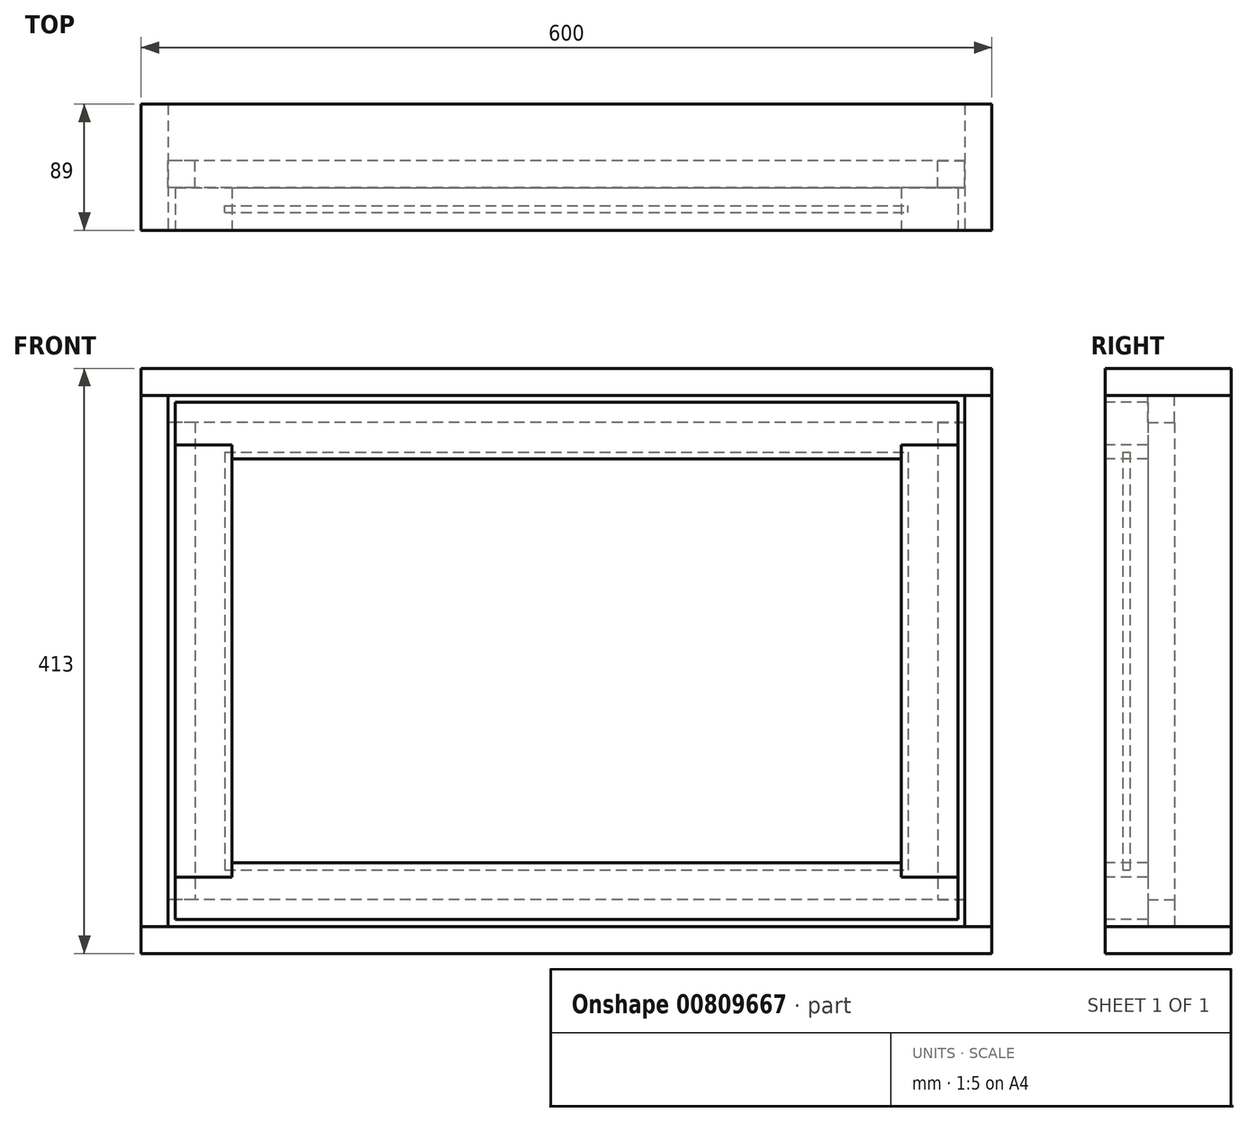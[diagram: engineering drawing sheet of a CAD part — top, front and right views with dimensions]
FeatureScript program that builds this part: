
annotation { "Feature Type Name" : "Feature", "Feature Type Description" : "" }
export const myFeature = defineFeature(function(context is Context, id is Id, definition is map)
    precondition{}
    {
        {
            assignVariable(context, id + "F0", {"name" : "D", "anyValue" : 89});
        }
        {
            var Q0;
            Q0=qCreatedBy(makeId("Front.planeOp"),FACE);
            var sketch = newSketch(context, id + "F1", { "sketchPlane" : qUnion([Q0])});
            skLineSegment(sketch, "E0.bottom", {"start": v(300, 206.5) * mm, "end": v(-300, 206.5) * mm});
            skLineSegment(sketch, "E0.top", {"start": v(300, -206.5) * mm, "end": v(-300, -206.5) * mm});
            skLineSegment(sketch, "E0.left", {"start": v(300, 206.5) * mm, "end": v(300, -206.5) * mm});
            skLineSegment(sketch, "E0.right", {"start": v(-300, 206.5) * mm, "end": v(-300, -206.5) * mm});
            skPoint(sketch, "E0.middle", {"position": v(0, 0) * mm});
            skSolve(sketch);
        }
        {
            var Q0;
            Q0=makeQuery(id+"F1.imprint","IMPRINT",FACE,{"disambiguationData":[TD([[makeQuery(id+"F1.imprint","IMPRINT",EDGE,{"derivedFrom":sQuery(id+"F1.wireOp",EDGE,"E0.bottom")}),1.0]])]});
            extrude(context, id + "F2", {"entities" : qUnion([Q0]), "oppositeDirection" : true, "depth" : (getVariable(context, 'D')) * mm, "offsetDistance" : 25 * mm});
        }
        {
            var Q0;
            Q0=makeQuery(id+"F2.opExtrude","CAP_FACE",FACE,{"disambiguationData":[OSD([sQuery(id+"F1.wireOp",EDGE,"E0.bottom"),sQuery(id+"F1.wireOp",EDGE,"E0.top"),sQuery(id+"F1.wireOp",EDGE,"E0.left"),sQuery(id+"F1.wireOp",EDGE,"E0.right")])],"isStart":true});
            var sketch = newSketch(context, id + "F3", { "sketchPlane" : qUnion([Q0])});
            skLineSegment(sketch, "E1.bottom", {"start": v(-300, -206.5) * mm, "end": v(300, -206.5) * mm});
            skLineSegment(sketch, "E1.top", {"start": v(-300, -187.5) * mm, "end": v(300, -187.5) * mm});
            skLineSegment(sketch, "E1.left", {"start": v(-300, -206.5) * mm, "end": v(-300, -187.5) * mm});
            skLineSegment(sketch, "E1.right", {"start": v(300, -206.5) * mm, "end": v(300, -187.5) * mm});
            skLineSegment(sketch, "E2.bottom", {"start": v(-300, 206.5) * mm, "end": v(300, 206.5) * mm});
            skLineSegment(sketch, "E2.top", {"start": v(-300, 187.5) * mm, "end": v(300, 187.5) * mm});
            skLineSegment(sketch, "E2.left", {"start": v(-300, 206.5) * mm, "end": v(-300, 187.5) * mm});
            skLineSegment(sketch, "E2.right", {"start": v(300, 206.5) * mm, "end": v(300, 187.5) * mm});
            skLineSegment(sketch, "E3.bottom", {"start": v(-300, 187.5) * mm, "end": v(-281, 187.5) * mm});
            skLineSegment(sketch, "E3.top", {"start": v(-300, -187.5) * mm, "end": v(-281, -187.5) * mm});
            skLineSegment(sketch, "E3.left", {"start": v(-300, 187.5) * mm, "end": v(-300, -187.5) * mm});
            skLineSegment(sketch, "E3.right", {"start": v(-281, 187.5) * mm, "end": v(-281, -187.5) * mm});
            skLineSegment(sketch, "E4.bottom", {"start": v(300, 187.5) * mm, "end": v(281, 187.5) * mm});
            skLineSegment(sketch, "E4.top", {"start": v(300, -187.5) * mm, "end": v(281, -187.5) * mm});
            skLineSegment(sketch, "E4.left", {"start": v(300, 187.5) * mm, "end": v(300, -187.5) * mm});
            skLineSegment(sketch, "E4.right", {"start": v(281, 187.5) * mm, "end": v(281, -187.5) * mm});
            skSolve(sketch);
        }
        {
            var Q0;
            Q0=makeQuery(id+"F3.imprint","IMPRINT",FACE,{"disambiguationData":[TD([[makeQuery(id+"F3.imprint","IMPRINT",EDGE,{"derivedFrom":sQuery(id+"F3.wireOp",EDGE,"E1.bottom")}),-1.0]])]});
            var Q1;
            Q1=makeQuery(id+"F2.opExtrude","CAP_FACE",FACE,{"disambiguationData":[OSD([sQuery(id+"F1.wireOp",EDGE,"E0.bottom"),sQuery(id+"F1.wireOp",EDGE,"E0.top"),sQuery(id+"F1.wireOp",EDGE,"E0.left"),sQuery(id+"F1.wireOp",EDGE,"E0.right")])],"isStart":false});
            extrude(context, id + "F4", {"entities" : qUnion([Q0]), "endBound" : BoundingType.UP_TO_SURFACE, "oppositeDirection" : true, "depth" : 25 * mm, "endBoundEntityFace" : qUnion([Q1]), "offsetDistance" : 25 * mm});
        }
        {
            var Q0;
            Q0=makeQuery(id+"F3.imprint","IMPRINT",FACE,{"disambiguationData":[TD([[makeQuery(id+"F3.imprint","IMPRINT",EDGE,{"derivedFrom":sQuery(id+"F3.wireOp",EDGE,"E2.bottom")}),1.0]])]});
            var Q1;
            Q1=makeQuery(id+"F2.opExtrude","CAP_FACE",FACE,{"disambiguationData":[OSD([sQuery(id+"F1.wireOp",EDGE,"E0.bottom"),sQuery(id+"F1.wireOp",EDGE,"E0.top"),sQuery(id+"F1.wireOp",EDGE,"E0.left"),sQuery(id+"F1.wireOp",EDGE,"E0.right")])],"isStart":false});
            extrude(context, id + "F5", {"entities" : qUnion([Q0]), "endBound" : BoundingType.UP_TO_SURFACE, "oppositeDirection" : true, "depth" : 25 * mm, "endBoundEntityFace" : qUnion([Q1]), "offsetDistance" : 25 * mm});
        }
        {
            var Q0;
            {var subQ2=sQuery(id+"F3.wireOp",EDGE,"E3.left");Q0=makeQuery(id+"F3.imprint","IMPRINT",FACE,{"disambiguationData":[TD([[makeQuery(id+"F3.imprint","IMPRINT",EDGE,{"derivedFrom":subQ2}),1.0]])]});}
            var Q1;
            Q1=makeQuery(id+"F2.opExtrude","CAP_FACE",FACE,{"disambiguationData":[OSD([sQuery(id+"F1.wireOp",EDGE,"E0.bottom"),sQuery(id+"F1.wireOp",EDGE,"E0.top"),sQuery(id+"F1.wireOp",EDGE,"E0.left"),sQuery(id+"F1.wireOp",EDGE,"E0.right")])],"isStart":false});
            extrude(context, id + "F6", {"entities" : qUnion([Q0]), "endBound" : BoundingType.UP_TO_SURFACE, "oppositeDirection" : true, "depth" : 25 * mm, "endBoundEntityFace" : qUnion([Q1]), "offsetDistance" : 25 * mm});
        }
        {
            var Q0;
            {var subQ0=sQuery(id+"F3.wireOp",EDGE,"E4.left");Q0=makeQuery(id+"F3.imprint","IMPRINT",FACE,{"disambiguationData":[TD([[makeQuery(id+"F3.imprint","IMPRINT",EDGE,{"derivedFrom":subQ0}),-1.0]])]});}
            var Q1;
            Q1=makeQuery(id+"F2.opExtrude","CAP_FACE",FACE,{"disambiguationData":[OSD([sQuery(id+"F1.wireOp",EDGE,"E0.bottom"),sQuery(id+"F1.wireOp",EDGE,"E0.top"),sQuery(id+"F1.wireOp",EDGE,"E0.left"),sQuery(id+"F1.wireOp",EDGE,"E0.right")])],"isStart":false});
            extrude(context, id + "F7", {"entities" : qUnion([Q0]), "endBound" : BoundingType.UP_TO_SURFACE, "oppositeDirection" : true, "depth" : 25 * mm, "endBoundEntityFace" : qUnion([Q1]), "offsetDistance" : 25 * mm});
        }
        {
            var Q0;
            Q0=qCreatedBy(makeId("Front.planeOp"),FACE);
            cPlane(context, id + "F8", {"entities" : qUnion([Q0]), "cplaneType" : CPlaneType.OFFSET, "offset" : 0 * mm, "width" : 150 * mm, "height" : 150 * mm});
        }
        {
            var Q0;
            Q0=qCreatedBy(id+"F8.planeOp",FACE);
            var sketch = newSketch(context, id + "F9", { "sketchPlane" : qUnion([Q0])});
            skLineSegment(sketch, "E5.bottom", {"start": v(-276, 182.5) * mm, "end": v(276, 182.5) * mm});
            skLineSegment(sketch, "E5.top", {"start": v(-276, -182.5) * mm, "end": v(276, -182.5) * mm});
            skLineSegment(sketch, "E5.left", {"start": v(-276, 182.5) * mm, "end": v(-276, -182.5) * mm});
            skLineSegment(sketch, "E5.right", {"start": v(276, 182.5) * mm, "end": v(276, -182.5) * mm});
            skLineSegment(sketch, "E6", {"start": v(-236, -142.5) * mm, "end": v(236, -142.5) * mm});
            skLineSegment(sketch, "E7", {"start": v(-236, 142.5) * mm, "end": v(236, 142.5) * mm});
            skLineSegment(sketch, "E8", {"start": v(276, 152.5) * mm, "end": v(236, 152.5) * mm});
            skLineSegment(sketch, "E9", {"start": v(236, 152.5) * mm, "end": v(236, -152.5) * mm});
            skLineSegment(sketch, "E10", {"start": v(236, -152.5) * mm, "end": v(276, -152.5) * mm});
            skLineSegment(sketch, "E11", {"start": v(-276, 152.5) * mm, "end": v(-236, 152.5) * mm});
            skLineSegment(sketch, "E12", {"start": v(-236, 152.5) * mm, "end": v(-236, -152.5) * mm});
            skLineSegment(sketch, "E13", {"start": v(-236, -152.5) * mm, "end": v(-276, -152.5) * mm});
            skSolve(sketch);
        }
        {
            var Q0;
            {var subQ2=sQuery(id+"F9.wireOp",EDGE,"E5.bottom");Q0=makeQuery(id+"F9.imprint","IMPRINT",FACE,{"disambiguationData":[TD([[makeQuery(id+"F9.imprint","IMPRINT",EDGE,{"derivedFrom":subQ2}),-1.0]])]});}
            extrude(context, id + "F10", {"entities" : qUnion([Q0]), "oppositeDirection" : true, "depth" : 30 * mm, "offsetDistance" : 25 * mm});
        }
        {
            var Q0;
            {var subQ3=sQuery(id+"F9.wireOp",EDGE,"E5.top");Q0=makeQuery(id+"F9.imprint","IMPRINT",FACE,{"disambiguationData":[TD([[makeQuery(id+"F9.imprint","IMPRINT",EDGE,{"derivedFrom":subQ3}),1.0]])]});}
            extrude(context, id + "F11", {"entities" : qUnion([Q0]), "oppositeDirection" : true, "depth" : 30 * mm, "offsetDistance" : 25 * mm});
        }
        {
            var Q0;
            {var subQ3=sQuery(id+"F9.wireOp",EDGE,"E11");Q0=makeQuery(id+"F9.imprint","IMPRINT",FACE,{"disambiguationData":[TD([[makeQuery(id+"F9.imprint","IMPRINT",EDGE,{"derivedFrom":subQ3}),-1.0]])]});}
            extrude(context, id + "F12", {"entities" : qUnion([Q0]), "oppositeDirection" : true, "depth" : 30 * mm, "offsetDistance" : 25 * mm});
        }
        {
            var Q0;
            {var subQ3=sQuery(id+"F9.wireOp",EDGE,"E8");Q0=makeQuery(id+"F9.imprint","IMPRINT",FACE,{"disambiguationData":[TD([[makeQuery(id+"F9.imprint","IMPRINT",EDGE,{"derivedFrom":subQ3}),1.0]])]});}
            extrude(context, id + "F13", {"entities" : qUnion([Q0]), "oppositeDirection" : true, "depth" : 30 * mm, "offsetDistance" : 25 * mm});
        }
        {
            var Q0;
            Q0=qCreatedBy(makeId("Front.planeOp"),FACE);
            cPlane(context, id + "F14", {"entities" : qUnion([Q0]), "cplaneType" : CPlaneType.OFFSET, "offset" : (30 / 2) * mm, "oppositeDirection" : true, "width" : 150 * mm, "height" : 150 * mm});
        }
        {
            var Q0;
            Q0=qCreatedBy(id+"F14.planeOp",FACE);
            var sketch = newSketch(context, id + "F15", { "sketchPlane" : qUnion([Q0])});
            skLineSegment(sketch, "E14.bottom", {"start": v(-241, 147.5) * mm, "end": v(241, 147.5) * mm});
            skLineSegment(sketch, "E14.top", {"start": v(-241, -147.5) * mm, "end": v(241, -147.5) * mm});
            skLineSegment(sketch, "E14.left", {"start": v(-241, 147.5) * mm, "end": v(-241, -147.5) * mm});
            skLineSegment(sketch, "E14.right", {"start": v(241, 147.5) * mm, "end": v(241, -147.5) * mm});
            skLineSegment(sketch, "E15.0", {"start": v(-236, 142.5) * mm, "end": v(236, 142.5) * mm});
            skSolve(sketch);
        }
        {
            var Q0;
            Q0=makeQuery(id+"F15.imprint","IMPRINT",FACE,{"disambiguationData":[TD([[makeQuery(id+"F15.imprint","IMPRINT",EDGE,{"derivedFrom":sQuery(id+"F15.wireOp",EDGE,"E14.bottom")}),-1.0]])]});
            extrude(context, id + "F16", {"entities" : qUnion([Q0]), "endBound" : BoundingType.SYMMETRIC, "depth" : 5 * mm, "offsetDistance" : 25 * mm});
        }
        {
            var Q0;
            Q0=makeQuery(id+"F4.opExtrude","SWEPT_FACE",FACE,{"disambiguationData":[OSD([sQuery(id+"F3.wireOp",EDGE,"E1.top")])]});
            var sketch = newSketch(context, id + "F17", { "sketchPlane" : qUnion([Q0])});
            skLineSegment(sketch, "E16.bottom", {"start": v(281, 30) * mm, "end": v(-281, 30) * mm});
            skLineSegment(sketch, "E16.top", {"start": v(281, 49) * mm, "end": v(-281, 49) * mm});
            skLineSegment(sketch, "E16.left", {"start": v(281, 30) * mm, "end": v(281, 49) * mm});
            skLineSegment(sketch, "E16.right", {"start": v(-281, 30) * mm, "end": v(-281, 49) * mm});
            skSolve(sketch);
        }
        {
            var Q0;
            Q0=makeQuery(id+"F17.imprint","IMPRINT",FACE,{"disambiguationData":[TD([[makeQuery(id+"F17.imprint","IMPRINT",EDGE,{"derivedFrom":sQuery(id+"F17.wireOp",EDGE,"E16.bottom")}),-1.0]])]});
            extrude(context, id + "F18", {"entities" : qUnion([Q0]), "depth" : 19 * mm, "offsetDistance" : 25 * mm});
        }
        {
            var Q0;
            Q0=makeQuery(id+"F18.opExtrude","SWEPT_BODY",BODY,{"disambiguationData":[OSD([sQuery(id+"F17.wireOp",EDGE,"E16.bottom"),sQuery(id+"F17.wireOp",EDGE,"E16.top"),sQuery(id+"F17.wireOp",EDGE,"E16.left"),sQuery(id+"F17.wireOp",EDGE,"E16.right")])]});
            var Q1;
            Q1=qCreatedBy(makeId("Top.planeOp"),FACE);
            mirror(context, id + "F19", {"entities" : qUnion([Q0]), "mirrorPlane" : qUnion([Q1])});
        }
        {
            var Q0;
            Q0=makeQuery(id+"F6.opExtrude","SWEPT_FACE",FACE,{"disambiguationData":[OSD([sQuery(id+"F3.wireOp",EDGE,"E3.right")])]});
            var sketch = newSketch(context, id + "F20", { "sketchPlane" : qUnion([Q0])});
            skLineSegment(sketch, "E17.bottom", {"start": v(30, 168.5) * mm, "end": v(49, 168.5) * mm});
            skLineSegment(sketch, "E17.top", {"start": v(30, -168.5) * mm, "end": v(49, -168.5) * mm});
            skLineSegment(sketch, "E17.left", {"start": v(30, 168.5) * mm, "end": v(30, -168.5) * mm});
            skLineSegment(sketch, "E17.right", {"start": v(49, 168.5) * mm, "end": v(49, -168.5) * mm});
            skSolve(sketch);
        }
        {
            var Q0;
            Q0=makeQuery(id+"F20.imprint","IMPRINT",FACE,{"disambiguationData":[TD([[makeQuery(id+"F20.imprint","IMPRINT",EDGE,{"derivedFrom":sQuery(id+"F20.wireOp",EDGE,"E17.bottom")}),-1.0]])]});
            extrude(context, id + "F21", {"entities" : qUnion([Q0]), "depth" : 19 * mm, "offsetDistance" : 25 * mm});
        }
        {
            var Q0;
            Q0=makeQuery(id+"F21.opExtrude","SWEPT_BODY",BODY,{"disambiguationData":[OSD([sQuery(id+"F20.wireOp",EDGE,"E17.bottom"),sQuery(id+"F20.wireOp",EDGE,"E17.top"),sQuery(id+"F20.wireOp",EDGE,"E17.left"),sQuery(id+"F20.wireOp",EDGE,"E17.right")])]});
            var Q1;
            Q1=qCreatedBy(makeId("Right.planeOp"),FACE);
            mirror(context, id + "F22", {"entities" : qUnion([Q0]), "mirrorPlane" : qUnion([Q1])});
        }
    });
